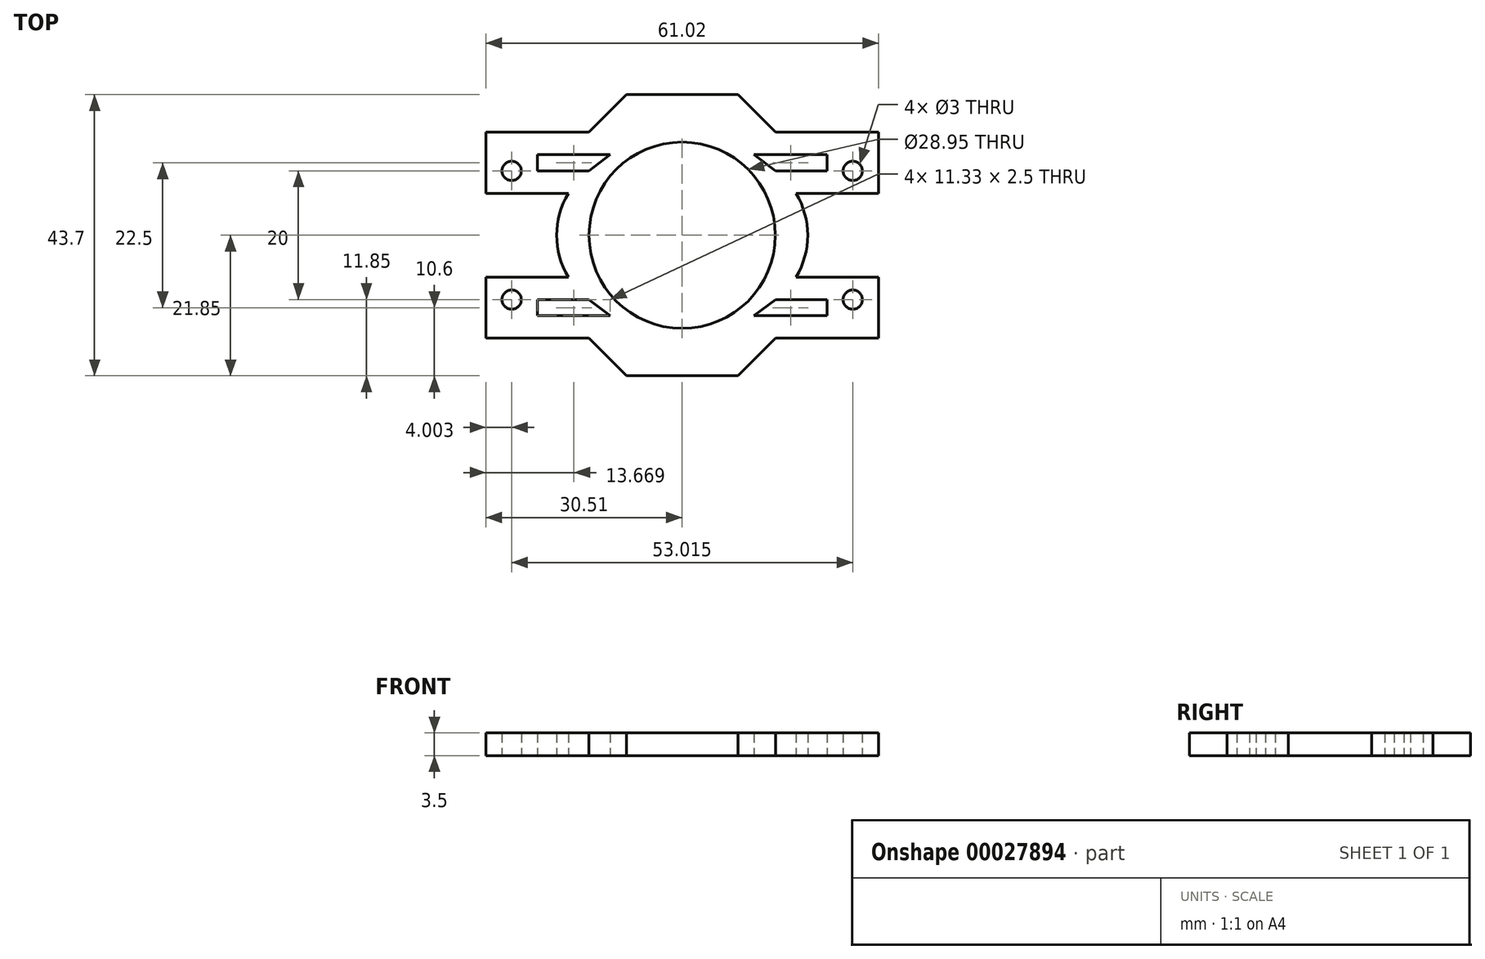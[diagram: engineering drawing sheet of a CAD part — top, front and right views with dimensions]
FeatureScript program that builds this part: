
annotation { "Feature Type Name" : "Feature", "Feature Type Description" : "" }
export const myFeature = defineFeature(function(context is Context, id is Id, definition is map)
    precondition{}
    {
        {
            var Q0;
            Q0=qCreatedBy(makeId("Top.planeOp"),FACE);
            var sketch = newSketch(context, id + "F0", { "sketchPlane" : qUnion([Q0])});
            skLineSegment(sketch, "E0.rect.bottom", {"start": v(30.5, 16) * mm, "end": v(-30.5, 16) * mm});
            skLineSegment(sketch, "E0.rect.top", {"start": v(30.5, -16) * mm, "end": v(-30.5, -16) * mm});
            skLineSegment(sketch, "E0.rect.left", {"start": v(30.5, 16) * mm, "end": v(30.5, -16) * mm});
            skLineSegment(sketch, "E0.rect.right", {"start": v(-30.5, 16) * mm, "end": v(-30.5, -16) * mm});
            skPoint(sketch, "E0.rect.middle", {"position": v(0, 0) * mm});
            skCircle(sketch, "E1", {"center": v(0, 0) * mm, "radius": 14.47 * mm});
            skLineSegment(sketch, "E2.rect.bottom", {"start": v(-19.5, -10) * mm, "end": v(-22.5, -10) * mm});
            skLineSegment(sketch, "E2.rect.top", {"start": v(-19.5, 10) * mm, "end": v(-22.5, 10) * mm});
            skLineSegment(sketch, "E2.rect.left", {"start": v(-19.5, -10) * mm, "end": v(-19.5, 10) * mm});
            skLineSegment(sketch, "E2.rect.right", {"start": v(-22.5, -10) * mm, "end": v(-22.5, 10) * mm});
            skPoint(sketch, "E2.rect.middle", {"position": v(-21, 0) * mm});
            skLineSegment(sketch, "E3.MirrorCS", {"start": v(19.5, 10) * mm, "end": v(22.5, 10) * mm});
            skLineSegment(sketch, "E4.MirrorCS", {"start": v(22.5, -10) * mm, "end": v(22.5, 10) * mm});
            skLineSegment(sketch, "E5.MirrorCS", {"start": v(19.5, -10) * mm, "end": v(22.5, -10) * mm});
            skLineSegment(sketch, "E6.MirrorCS", {"start": v(19.5, -10) * mm, "end": v(19.5, 10) * mm});
            skCircle(sketch, "E7", {"center": v(-26.5, 10) * mm, "radius": 1.5 * mm});
            skCircle(sketch, "E8", {"center": v(-26.5, -10) * mm, "radius": 1.5 * mm});
            skCircle(sketch, "E9.MirrorC", {"center": v(26.5, 10) * mm, "radius": 1.5 * mm});
            skCircle(sketch, "E10.MirrorC", {"center": v(26.5, -10) * mm, "radius": 1.5 * mm});
            skLineSegment(sketch, "E11", {"start": v(-19.5, -10) * mm, "end": v(-14.5, -10) * mm});
            skLineSegment(sketch, "E12", {"start": v(-19.5, 10) * mm, "end": v(-14.5, 10) * mm});
            skArc(sketch, "E13", {"start": v(-14.5, 10) * mm, "mid": v(-19.5, 0) * mm, "end": v(-14.5, -10) * mm});
            skArc(sketch, "E14.MirrorCS", {"start": v(14.5, 10) * mm, "mid": v(19.5, 0) * mm, "end": v(14.5, -10) * mm});
            skLineSegment(sketch, "E15.MirrorCS", {"start": v(19.5, -10) * mm, "end": v(14.5, -10) * mm});
            skLineSegment(sketch, "E16.MirrorCS", {"start": v(19.5, 10) * mm, "end": v(14.5, 10) * mm});
            skLineSegment(sketch, "E17", {"start": v(-22.5, 6.5) * mm, "end": v(-19.5, 6.5) * mm});
            skLineSegment(sketch, "E18", {"start": v(-22.5, -6.5) * mm, "end": v(-19.5, -6.5) * mm});
            skLineSegment(sketch, "E19", {"start": v(-19.5, -6.5) * mm, "end": v(-17.69, -6.5) * mm});
            skLineSegment(sketch, "E20", {"start": v(-19.5, 6.5) * mm, "end": v(-17.69, 6.5) * mm});
            skLineSegment(sketch, "E21.bottom", {"start": v(-22.5, 6.5) * mm, "end": v(-30.5, 6.5) * mm});
            skLineSegment(sketch, "E21.top", {"start": v(-22.5, -6.5) * mm, "end": v(-30.5, -6.5) * mm});
            skLineSegment(sketch, "E21.left", {"start": v(-22.5, 6.5) * mm, "end": v(-22.5, -6.5) * mm});
            skLineSegment(sketch, "E21.right", {"start": v(-30.5, 6.5) * mm, "end": v(-30.5, -6.5) * mm});
            skLineSegment(sketch, "E22.MirrorCS", {"start": v(19.5, 6.5) * mm, "end": v(17.69, 6.5) * mm});
            skLineSegment(sketch, "E23.MirrorCS", {"start": v(22.5, 6.5) * mm, "end": v(19.5, 6.5) * mm});
            skLineSegment(sketch, "E24.MirrorCS", {"start": v(22.5, 6.5) * mm, "end": v(30.5, 6.5) * mm});
            skLineSegment(sketch, "E25.MirrorCS", {"start": v(22.5, -6.5) * mm, "end": v(30.5, -6.5) * mm});
            skLineSegment(sketch, "E26.MirrorCS", {"start": v(22.5, -6.5) * mm, "end": v(19.5, -6.5) * mm});
            skLineSegment(sketch, "E27.MirrorCS", {"start": v(19.5, -6.5) * mm, "end": v(17.69, -6.5) * mm});
            skLineSegment(sketch, "E28", {"start": v(-14.5, -16) * mm, "end": v(-8.66, -21.85) * mm});
            skLineSegment(sketch, "E29", {"start": v(-8.66, -21.85) * mm, "end": v(8.66, -21.85) * mm});
            skLineSegment(sketch, "E30", {"start": v(8.66, -21.85) * mm, "end": v(14.5, -16) * mm});
            skLineSegment(sketch, "E31.MirrorCS", {"start": v(-8.66, -21.85) * mm, "end": v(-8.66, -39.17) * mm});
            skLineSegment(sketch, "E32.MirrorCS", {"start": v(-14.5, 16) * mm, "end": v(-8.66, 21.85) * mm});
            skLineSegment(sketch, "E33.MirrorCS", {"start": v(-8.66, 21.85) * mm, "end": v(8.66, 21.85) * mm});
            skLineSegment(sketch, "E34.MirrorCS", {"start": v(8.66, 21.85) * mm, "end": v(14.5, 16) * mm});
            skLineSegment(sketch, "E35.bottom", {"start": v(-14.5, -10) * mm, "end": v(-22.5, -10) * mm});
            skLineSegment(sketch, "E35.top", {"start": v(-14.5, -12.5) * mm, "end": v(-22.5, -12.5) * mm});
            skLineSegment(sketch, "E35.left", {"start": v(-14.5, -10) * mm, "end": v(-14.5, -12.5) * mm});
            skLineSegment(sketch, "E35.right", {"start": v(-22.5, -10) * mm, "end": v(-22.5, -12.5) * mm});
            skLineSegment(sketch, "E36", {"start": v(30.5, 0) * mm, "end": v(-30.5, 0) * mm, "construction": true});
            skLineSegment(sketch, "E37", {"start": v(0, -21.85) * mm, "end": v(0, 21.85) * mm, "construction": true});
            skLineSegment(sketch, "E38.MirrorCS", {"start": v(-14.5, 12.5) * mm, "end": v(-22.5, 12.5) * mm});
            skLineSegment(sketch, "E39.MirrorCS", {"start": v(-22.5, 10) * mm, "end": v(-22.5, 12.5) * mm});
            skLineSegment(sketch, "E40.MirrorCS", {"start": v(-14.5, 10) * mm, "end": v(-14.5, 12.5) * mm});
            skLineSegment(sketch, "E41.MirrorCS", {"start": v(-45.02, -21.85) * mm, "end": v(-45.02, 21.85) * mm});
            skLineSegment(sketch, "E42.MirrorCS", {"start": v(14.5, 10) * mm, "end": v(14.5, 12.5) * mm});
            skLineSegment(sketch, "E43.MirrorCS", {"start": v(14.5, 12.5) * mm, "end": v(22.5, 12.5) * mm});
            skLineSegment(sketch, "E44.MirrorCS", {"start": v(22.5, 10) * mm, "end": v(22.5, 12.5) * mm});
            skLineSegment(sketch, "E45.MirrorCS", {"start": v(22.5, -10) * mm, "end": v(22.5, -12.5) * mm});
            skLineSegment(sketch, "E46.MirrorCS", {"start": v(14.5, -12.5) * mm, "end": v(22.5, -12.5) * mm});
            skLineSegment(sketch, "E47.MirrorCS", {"start": v(14.5, -10) * mm, "end": v(14.5, -12.5) * mm});
            skLineSegment(sketch, "E48", {"start": v(-14.5, -12.5) * mm, "end": v(-12, -12.5) * mm});
            skLineSegment(sketch, "E49", {"start": v(-14.5, -10) * mm, "end": v(-11.18, -12.5) * mm});
            skLineSegment(sketch, "E50", {"start": v(-11.18, -12.5) * mm, "end": v(-12, -12.5) * mm});
            skLineSegment(sketch, "E51.MirrorCS", {"start": v(14.5, -12.5) * mm, "end": v(12, -12.5) * mm});
            skLineSegment(sketch, "E52.MirrorCS", {"start": v(11.18, -12.5) * mm, "end": v(12, -12.5) * mm});
            skLineSegment(sketch, "E53.MirrorCS", {"start": v(14.5, -10) * mm, "end": v(11.18, -12.5) * mm});
            skLineSegment(sketch, "E54.MirrorCS", {"start": v(14.5, 12.5) * mm, "end": v(12, 12.5) * mm});
            skLineSegment(sketch, "E55.MirrorCS", {"start": v(11.18, 12.5) * mm, "end": v(12, 12.5) * mm});
            skLineSegment(sketch, "E56.MirrorCS", {"start": v(14.5, 10) * mm, "end": v(11.18, 12.5) * mm});
            skLineSegment(sketch, "E57.MirrorCS", {"start": v(-14.5, 12.5) * mm, "end": v(-12, 12.5) * mm});
            skLineSegment(sketch, "E58.MirrorCS", {"start": v(-11.18, 12.5) * mm, "end": v(-12, 12.5) * mm});
            skLineSegment(sketch, "E59.MirrorCS", {"start": v(-14.5, 10) * mm, "end": v(-11.18, 12.5) * mm});
            skSolve(sketch);
        }
        {
            var Q0;
            Q0=makeQuery(id+"F0.imprint","IMPRINT",FACE,{"disambiguationData":[TD([[makeQuery(id+"F0.imprint","IMPRINT",EDGE,{"derivedFrom":sQuery(id+"F0.wireOp",EDGE,"E0.rect.bottom")}),1.0]])]});
            var Q1;
            {var subQ2=sQuery(id+"F0.wireOp",EDGE,"E2.rect.top");Q1=makeQuery(id+"F0.imprint","IMPRINT",FACE,{"disambiguationData":[TD([[makeQuery(id+"F0.imprint","IMPRINT",EDGE,{"derivedFrom":subQ2}),1.0]])]});}
            var Q2;
            {var subQ2=sQuery(id+"F0.wireOp",EDGE,"E12");Q2=makeQuery(id+"F0.imprint","IMPRINT",FACE,{"disambiguationData":[TD([[makeQuery(id+"F0.imprint","IMPRINT",EDGE,{"derivedFrom":subQ2}),-1.0]])]});}
            var Q3;
            {var subQ2=sQuery(id+"F0.wireOp",EDGE,"E2.rect.bottom");Q3=makeQuery(id+"F0.imprint","IMPRINT",FACE,{"disambiguationData":[TD([[makeQuery(id+"F0.imprint","IMPRINT",EDGE,{"derivedFrom":subQ2}),-1.0]])]});}
            var Q4;
            {var subQ2=sQuery(id+"F0.wireOp",EDGE,"E11");Q4=makeQuery(id+"F0.imprint","IMPRINT",FACE,{"disambiguationData":[TD([[makeQuery(id+"F0.imprint","IMPRINT",EDGE,{"derivedFrom":subQ2}),1.0]])]});}
            var Q5;
            {var subQ2=sQuery(id+"F0.wireOp",EDGE,"E16.MirrorCS");Q5=makeQuery(id+"F0.imprint","IMPRINT",FACE,{"disambiguationData":[TD([[makeQuery(id+"F0.imprint","IMPRINT",EDGE,{"derivedFrom":subQ2}),1.0]])]});}
            var Q6;
            {var subQ2=sQuery(id+"F0.wireOp",EDGE,"E3.MirrorCS");Q6=makeQuery(id+"F0.imprint","IMPRINT",FACE,{"disambiguationData":[TD([[makeQuery(id+"F0.imprint","IMPRINT",EDGE,{"derivedFrom":subQ2}),-1.0]])]});}
            var Q7;
            {var subQ1=sQuery(id+"F0.wireOp",EDGE,"E15.MirrorCS");Q7=makeQuery(id+"F0.imprint","IMPRINT",FACE,{"disambiguationData":[TD([[makeQuery(id+"F0.imprint","IMPRINT",EDGE,{"derivedFrom":subQ1}),-1.0]])]});}
            var Q8;
            {var subQ2=sQuery(id+"F0.wireOp",EDGE,"E5.MirrorCS");Q8=makeQuery(id+"F0.imprint","IMPRINT",FACE,{"disambiguationData":[TD([[makeQuery(id+"F0.imprint","IMPRINT",EDGE,{"derivedFrom":subQ2}),1.0]])]});}
            var Q9;
            {var subQ1=sQuery(id+"F0.wireOp",EDGE,"E28");Q9=makeQuery(id+"F0.imprint","IMPRINT",FACE,{"disambiguationData":[TD([[makeQuery(id+"F0.imprint","IMPRINT",EDGE,{"derivedFrom":subQ1}),1.0]])]});}
            var Q10;
            {var subQ1=sQuery(id+"F0.wireOp",EDGE,"E32.MirrorCS");Q10=makeQuery(id+"F0.imprint","IMPRINT",FACE,{"disambiguationData":[TD([[makeQuery(id+"F0.imprint","IMPRINT",EDGE,{"derivedFrom":subQ1}),-1.0]])]});}
            var Q11;
            {var subQ5=sQuery(id+"F0.wireOp",EDGE,"E18");Q11=makeQuery(id+"F0.imprint","IMPRINT",FACE,{"disambiguationData":[TD([[makeQuery(id+"F0.imprint","IMPRINT",EDGE,{"derivedFrom":subQ5}),-1.0]])]});}
            var Q12;
            {var subQ5=sQuery(id+"F0.wireOp",EDGE,"E19");Q12=makeQuery(id+"F0.imprint","IMPRINT",FACE,{"disambiguationData":[TD([[makeQuery(id+"F0.imprint","IMPRINT",EDGE,{"derivedFrom":subQ5}),-1.0]])]});}
            extrude(context, id + "F1", {"entities" : qUnion([Q0, Q1, Q2, Q3, Q4, Q5, Q6, Q7, Q8, Q9, Q10, Q11, Q12]), "depth" : 3.5 * mm});
        }
    });
